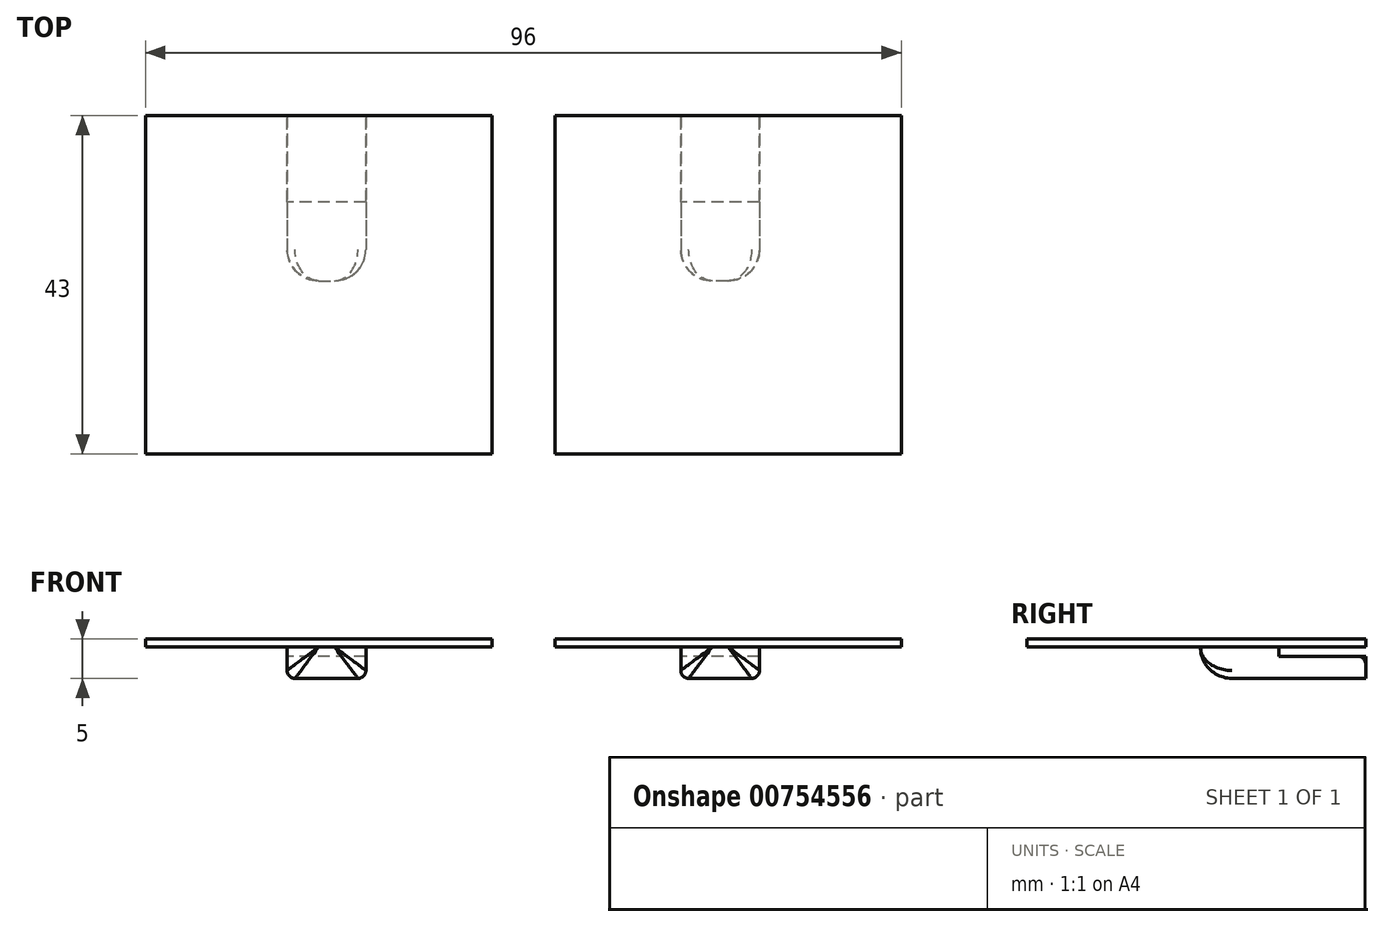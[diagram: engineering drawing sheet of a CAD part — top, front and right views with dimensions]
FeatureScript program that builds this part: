
annotation { "Feature Type Name" : "Feature", "Feature Type Description" : "" }
export const myFeature = defineFeature(function(context is Context, id is Id, definition is map)
    precondition{}
    {
        {
            var Q0;
            Q0=qCreatedBy(makeId("Top.planeOp"),FACE);
            var sketch = newSketch(context, id + "F0", { "sketchPlane" : qUnion([Q0])});
            skLineSegment(sketch, "E0.bottom", {"start": v(-48, 43) * mm, "end": v(-4, 43) * mm});
            skLineSegment(sketch, "E0.top", {"start": v(-48, 0) * mm, "end": v(-4, 0) * mm});
            skLineSegment(sketch, "E0.left", {"start": v(-48, 43) * mm, "end": v(-48, 0) * mm});
            skLineSegment(sketch, "E0.right", {"start": v(-4, 43) * mm, "end": v(-4, 0) * mm});
            skLineSegment(sketch, "E1.bottom", {"start": v(-30, 43) * mm, "end": v(-20, 43) * mm});
            skLineSegment(sketch, "E1.top", {"start": v(-30, 22) * mm, "end": v(-20, 22) * mm});
            skLineSegment(sketch, "E1.left", {"start": v(-30, 43) * mm, "end": v(-30, 22) * mm});
            skLineSegment(sketch, "E1.right", {"start": v(-20, 43) * mm, "end": v(-20, 22) * mm});
            skLineSegment(sketch, "E2.MirrorCS", {"start": v(48, 43) * mm, "end": v(4, 43) * mm});
            skLineSegment(sketch, "E3.MirrorCS", {"start": v(48, 0) * mm, "end": v(4, 0) * mm});
            skLineSegment(sketch, "E4.MirrorCS", {"start": v(48, 43) * mm, "end": v(48, 0) * mm});
            skLineSegment(sketch, "E5.MirrorCS", {"start": v(4, 43) * mm, "end": v(4, 0) * mm});
            skLineSegment(sketch, "E6.MirrorCS", {"start": v(30, 43) * mm, "end": v(20, 43) * mm});
            skLineSegment(sketch, "E7.MirrorCS", {"start": v(30, 22) * mm, "end": v(20, 22) * mm});
            skLineSegment(sketch, "E8.MirrorCS", {"start": v(20, 43) * mm, "end": v(20, 22) * mm});
            skLineSegment(sketch, "E9.MirrorCS", {"start": v(30, 43) * mm, "end": v(30, 22) * mm});
            skSolve(sketch);
        }
        {
            var Q0;
            Q0=makeQuery(id+"F0.imprint","IMPRINT",FACE,{"disambiguationData":[TD([[makeQuery(id+"F0.imprint","IMPRINT",EDGE,{"derivedFrom":sQuery(id+"F0.wireOp",EDGE,"E0.top")}),1.0]])]});
            var Q1;
            Q1=makeQuery(id+"F0.imprint","IMPRINT",FACE,{"disambiguationData":[TD([[makeQuery(id+"F0.imprint","IMPRINT",EDGE,{"derivedFrom":sQuery(id+"F0.wireOp",EDGE,"E1.top")}),1.0]])]});
            var Q2;
            Q2=makeQuery(id+"F0.imprint","IMPRINT",FACE,{"disambiguationData":[TD([[makeQuery(id+"F0.imprint","IMPRINT",EDGE,{"derivedFrom":sQuery(id+"F0.wireOp",EDGE,"E3.MirrorCS")}),-1.0]])]});
            var Q3;
            Q3=makeQuery(id+"F0.imprint","IMPRINT",FACE,{"disambiguationData":[TD([[makeQuery(id+"F0.imprint","IMPRINT",EDGE,{"derivedFrom":sQuery(id+"F0.wireOp",EDGE,"E7.MirrorCS")}),-1.0]])]});
            extrude(context, id + "F1", {"entities" : qUnion([Q0, Q1, Q2, Q3]), "depth" : 1 * mm, "offsetDistance" : 25 * mm});
        }
        {
            var Q0;
            Q0=makeQuery(id+"F0.imprint","IMPRINT",FACE,{"disambiguationData":[TD([[makeQuery(id+"F0.imprint","IMPRINT",EDGE,{"derivedFrom":sQuery(id+"F0.wireOp",EDGE,"E7.MirrorCS")}),-1.0]])]});
            var Q1;
            Q1=makeQuery(id+"F0.imprint","IMPRINT",FACE,{"disambiguationData":[TD([[makeQuery(id+"F0.imprint","IMPRINT",EDGE,{"derivedFrom":sQuery(id+"F0.wireOp",EDGE,"E1.top")}),1.0]])]});
            extrude(context, id + "F2", {"entities" : qUnion([Q0, Q1]), "operationType" : NewBodyOperationType.ADD, "oppositeDirection" : true, "depth" : 4 * mm, "offsetDistance" : 25 * mm});
        }
        {
            var Q0;
            {var subQ0=sQuery(id+"F0.wireOp",EDGE,"E2.MirrorCS");Q0=makeQuery(id+"F2.boolean.opBoolean","MERGE",FACE,{"derivedFrom":[makeQuery(id+"F1.opExtrude","SWEPT_FACE",FACE,{"disambiguationData":[OSD([subQ0])]}),makeQuery(id+"F2.opExtrude","SWEPT_FACE",FACE,{"disambiguationData":[OSD([subQ0])]})]});}
            var sketch = newSketch(context, id + "F3", { "sketchPlane" : qUnion([Q0])});
            skLineSegment(sketch, "E10.bottom", {"start": v(-30, 0) * mm, "end": v(-20, 0) * mm});
            skLineSegment(sketch, "E10.top", {"start": v(-30, -1.2) * mm, "end": v(-20, -1.2) * mm});
            skLineSegment(sketch, "E10.left", {"start": v(-30, 0) * mm, "end": v(-30, -1.2) * mm});
            skLineSegment(sketch, "E10.right", {"start": v(-20, 0) * mm, "end": v(-20, -1.2) * mm});
            skSolve(sketch);
        }
        {
            var Q0;
            {var subQ0=sQuery(id+"F0.wireOp",EDGE,"E0.bottom");Q0=makeQuery(id+"F2.boolean.opBoolean","MERGE",FACE,{"derivedFrom":[makeQuery(id+"F1.opExtrude","SWEPT_FACE",FACE,{"disambiguationData":[OSD([subQ0])]}),makeQuery(id+"F2.opExtrude","SWEPT_FACE",FACE,{"disambiguationData":[OSD([subQ0])]})]});}
            var sketch = newSketch(context, id + "F4", { "sketchPlane" : qUnion([Q0])});
            skLineSegment(sketch, "E11.bottom", {"start": v(20, 0) * mm, "end": v(30, 0) * mm});
            skLineSegment(sketch, "E11.top", {"start": v(20, -1.2) * mm, "end": v(30, -1.2) * mm});
            skLineSegment(sketch, "E11.left", {"start": v(20, 0) * mm, "end": v(20, -1.2) * mm});
            skLineSegment(sketch, "E11.right", {"start": v(30, 0) * mm, "end": v(30, -1.2) * mm});
            skSolve(sketch);
        }
        {
            var Q0;
            Q0=makeQuery(id+"F3.imprint","IMPRINT",FACE,{"disambiguationData":[TD([[makeQuery(id+"F3.imprint","IMPRINT",EDGE,{"derivedFrom":sQuery(id+"F3.wireOp",EDGE,"E10.bottom")}),-1.0]])]});
            var Q1;
            Q1=makeQuery(id+"F4.imprint","IMPRINT",FACE,{"disambiguationData":[TD([[makeQuery(id+"F4.imprint","IMPRINT",EDGE,{"derivedFrom":sQuery(id+"F4.wireOp",EDGE,"E11.bottom")}),-1.0]])]});
            extrude(context, id + "F5", {"entities" : qUnion([Q0, Q1]), "operationType" : NewBodyOperationType.REMOVE, "oppositeDirection" : true, "depth" : 11 * mm, "offsetDistance" : 25 * mm});
        }
        {
            var Q0;
            Q0=makeQuery(id+"F2.opExtrude","CAP_EDGE",EDGE,{"disambiguationData":[OSD([sQuery(id+"F0.wireOp",EDGE,"E9.MirrorCS")])],"isStart":false});
            var Q1;
            Q1=makeQuery(id+"F2.opExtrude","CAP_EDGE",EDGE,{"disambiguationData":[OSD([sQuery(id+"F0.wireOp",EDGE,"E8.MirrorCS")])],"isStart":false});
            var Q2;
            Q2=makeQuery(id+"F2.opExtrude","CAP_EDGE",EDGE,{"disambiguationData":[OSD([sQuery(id+"F0.wireOp",EDGE,"E1.right")])],"isStart":false});
            var Q3;
            Q3=makeQuery(id+"F2.opExtrude","CAP_EDGE",EDGE,{"disambiguationData":[OSD([sQuery(id+"F0.wireOp",EDGE,"E1.left")])],"isStart":false});
            var Q4;
            Q4=makeQuery(id+"F5.boolean.opBoolean","COPY",EDGE,{"derivedFrom":makeQuery(id+"F5.opExtrude","CAP_EDGE",EDGE,{"disambiguationData":[OSD([sQuery(id+"F3.wireOp",EDGE,"E10.top")])],"isStart":true})});
            var Q5;
            Q5=makeQuery(id+"F5.boolean.opBoolean","COPY",EDGE,{"derivedFrom":makeQuery(id+"F5.opExtrude","CAP_EDGE",EDGE,{"disambiguationData":[OSD([sQuery(id+"F4.wireOp",EDGE,"E11.top")])],"isStart":true})});
            fillet(context, id + "F6", {"entities" : qUnion([Q0, Q1, Q2, Q3, Q4, Q5]), "radius" : 1 * mm, "tangentPropagation" : true, "allowEdgeOverflow" : false});
        }
        {
            var Q0;
            Q0=makeQuery(id+"F2.opExtrude","CAP_EDGE",EDGE,{"disambiguationData":[OSD([sQuery(id+"F0.wireOp",EDGE,"E7.MirrorCS")])],"isStart":false});
            var Q1;
            Q1=makeQuery(id+"F2.opExtrude","CAP_EDGE",EDGE,{"disambiguationData":[OSD([sQuery(id+"F0.wireOp",EDGE,"E1.top")])],"isStart":false});
            fillet(context, id + "F7", {"entities" : qUnion([Q0, Q1]), "radius" : 4 * mm, "tangentPropagation" : true, "allowEdgeOverflow" : false});
        }
    });
